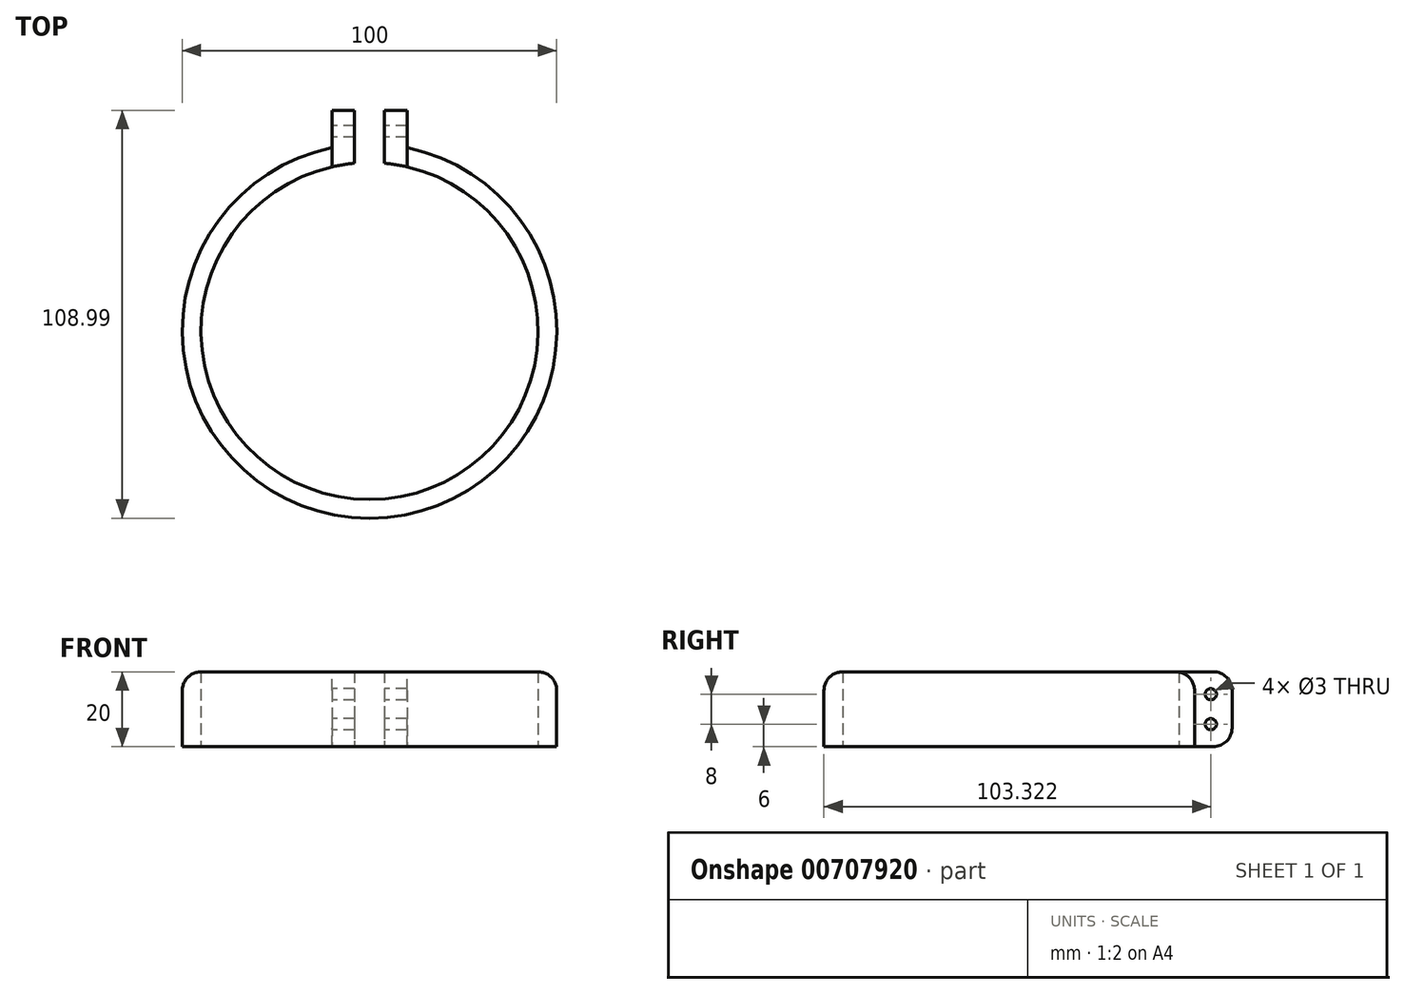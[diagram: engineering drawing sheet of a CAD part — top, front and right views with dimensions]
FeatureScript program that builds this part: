
annotation { "Feature Type Name" : "Feature", "Feature Type Description" : "" }
export const myFeature = defineFeature(function(context is Context, id is Id, definition is map)
    precondition{}
    {
        {
            var Q0;
            Q0=qCreatedBy(makeId("Top.planeOp"),FACE);
            var sketch = newSketch(context, id + "F0", { "sketchPlane" : qUnion([Q0])});
            skLineSegment(sketch, "E0", {"start": v(-4, 44.82) * mm, "end": v(-4, 58.99) * mm});
            skLineSegment(sketch, "E1", {"start": v(-4, 58.99) * mm, "end": v(-10, 58.99) * mm});
            skLineSegment(sketch, "E2", {"start": v(-10, 58.99) * mm, "end": v(-10, 48.99) * mm});
            skLineSegment(sketch, "E3", {"start": v(4, 44.82) * mm, "end": v(4, 58.99) * mm});
            skLineSegment(sketch, "E4", {"start": v(4, 58.99) * mm, "end": v(10, 58.99) * mm});
            skLineSegment(sketch, "E5", {"start": v(10, 58.99) * mm, "end": v(10, 48.99) * mm});
            skArc(sketch, "E6", {"start": v(-4, 44.82) * mm, "mid": v(0, -45) * mm, "end": v(4, 44.82) * mm});
            skArc(sketch, "E7", {"start": v(-10, 48.99) * mm, "mid": v(0, -50) * mm, "end": v(10, 48.99) * mm});
            skSolve(sketch);
        }
        {
            var Q0;
            Q0 = qSketchRegion(id + "F0", true);
            extrude(context, id + "F1", {"entities" : qUnion([Q0]), "depth" : 20 * mm, "offsetDistance" : 25 * mm});
        }
        {
            var Q0;
            Q0=makeQuery(id+"F1.opExtrude","SWEPT_FACE",FACE,{"disambiguationData":[OSD([sQuery(id+"F0.wireOp",EDGE,"E2")])]});
            var sketch = newSketch(context, id + "F2", { "sketchPlane" : qUnion([Q0])});
            skCircle(sketch, "E8", {"center": v(-53.32, 14) * mm, "radius": 1.5 * mm});
            skCircle(sketch, "E9", {"center": v(-53.32, 6) * mm, "radius": 1.5 * mm});
            skLineSegment(sketch, "E10", {"start": v(-53.32, 14) * mm, "end": v(-53.32, 20) * mm, "construction": true});
            skLineSegment(sketch, "E11", {"start": v(-53.32, 14) * mm, "end": v(-53.32, 6) * mm, "construction": true});
            skLineSegment(sketch, "E12", {"start": v(-53.32, 6) * mm, "end": v(-53.32, 0) * mm, "construction": true});
            skLineSegment(sketch, "E13.0", {"start": v(-44.82, 20) * mm, "end": v(-44.82, 0) * mm, "construction": true});
            skLineSegment(sketch, "E14.0", {"start": v(-48.99, 20) * mm, "end": v(-48.99, 0) * mm, "construction": true});
            skLineSegment(sketch, "E15.0", {"start": v(-58.99, 20) * mm, "end": v(-58.99, 0) * mm, "construction": true});
            skSolve(sketch);
        }
        {
            var Q0;
            Q0 = qSketchRegion(id + "F2", true);
            var Q1;
            Q1=makeQuery(id+"F1.opExtrude","SWEPT_FACE",FACE,{"disambiguationData":[OSD([sQuery(id+"F0.wireOp",EDGE,"E5")])]});
            extrude(context, id + "F3", {"entities" : qUnion([Q0]), "operationType" : NewBodyOperationType.REMOVE, "endBound" : BoundingType.UP_TO_SURFACE, "oppositeDirection" : true, "depth" : 25 * mm, "endBoundEntityFace" : qUnion([Q1]), "offsetDistance" : 25 * mm});
        }
        {
            var Q0;
            Q0=makeQuery(id+"F1.opExtrude","CAP_EDGE",EDGE,{"disambiguationData":[OSD([sQuery(id+"F0.wireOp",EDGE,"E1")])],"isStart":true});
            var Q1;
            Q1=makeQuery(id+"F1.opExtrude","CAP_EDGE",EDGE,{"disambiguationData":[OSD([sQuery(id+"F0.wireOp",EDGE,"E4")])],"isStart":true});
            var Q2;
            Q2=makeQuery(id+"F1.opExtrude","CAP_EDGE",EDGE,{"disambiguationData":[OSD([sQuery(id+"F0.wireOp",EDGE,"E1")])],"isStart":false});
            var Q3;
            Q3=makeQuery(id+"F1.opExtrude","CAP_EDGE",EDGE,{"disambiguationData":[OSD([sQuery(id+"F0.wireOp",EDGE,"E4")])],"isStart":false});
            var Q4;
            Q4=makeQuery(id+"F1.opExtrude","CAP_EDGE",EDGE,{"disambiguationData":[OSD([sQuery(id+"F0.wireOp",EDGE,"E7")])],"isStart":false});
            fillet(context, id + "F4", {"entities" : qUnion([Q0, Q1, Q2, Q3, Q4]), "radius" : 5 * mm, "tangentPropagation" : true, "allowEdgeOverflow" : false});
        }
    });
